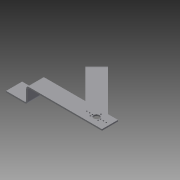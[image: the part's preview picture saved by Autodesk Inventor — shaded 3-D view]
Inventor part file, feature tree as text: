
AUTODESK INVENTOR PART (.ipt)
format: ipt  version: 2013 (Build 170138000, 138)  size: 183,808 bytes
history: native  units: in
note: dims shown in document units (in); Inventor stores cm internally (conversion verified against a paired STEP export)
features: sheet_metal_op x7, sketch x5, other x5
ambient origin geometry x8: Origin, YZ Plane, XZ Plane, XY Plane, X Axis, Y Axis, Z Axis, Center Point
bodies: Solid1 (feature_tree)
feature tree (17):
  sheet_metal_op  "Face1"
  sheet_metal_op  "Flange3"
  sheet_metal_op  "Flange4"
  sketch  "Sketch1"  dims[d5=3.0in]
  other  "Plate1"
  sketch  "Sketch4"  dims[d7=0.75in]
  other  "Plate4"
  sheet_metal_op  "Bend3"
  sheet_metal_op  "Corner3"
  sketch  "Sketch5"  dims[d8=0.125in]
  other  "Plate5"
  sheet_metal_op  "Bend4"
  sheet_metal_op  "Corner4"
  sketch  "Sketch6"  dims[d34=1.5in]
  sketch  "Sketch7"  dims[d35=1.5in d36=0.75in d37=0.75in d39=45.0deg d41=4.0in d42=4.0in d43=0.75in d44=1.25in d45=0.125in d46=0.0625in d47=0.25in d48=0.125in d49=2.0in d50=90.0deg d51=0.125in d52=0.5in d53=0.125in d54=0.125in d55=0.125in d56=0.0625in d57=0.25in d58=0.125in d59=2.0in d60=90.0deg d61=0.125in d62=0.5in d63=0.125in d64=0.125in d65=0.266in d66=0.266in d67=0.25in d68=0.75in d69=0.75in d70=0.25in d71=0.125in d72=0.0in d73=0.266in d74=0.266in d75=0.25in d76=0.75in d77=0.75in d78=0.25in d79=0.125in d80=0.0in]
  other  "Cut1"
  other  "Cut2"
